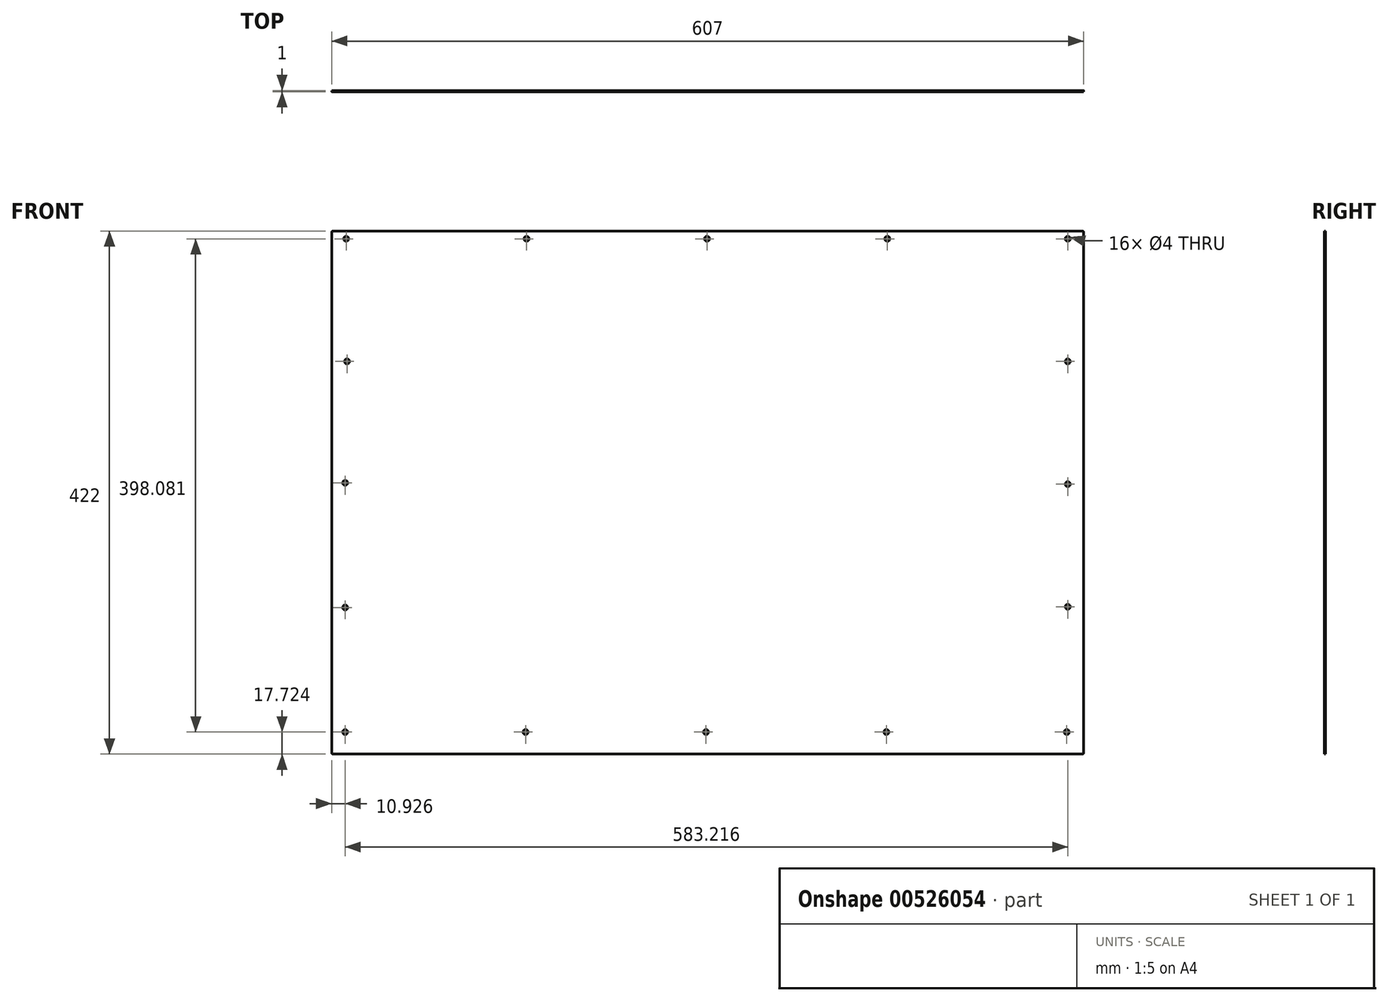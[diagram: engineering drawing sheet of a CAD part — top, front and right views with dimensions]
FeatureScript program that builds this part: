
annotation { "Feature Type Name" : "Feature", "Feature Type Description" : "" }
export const myFeature = defineFeature(function(context is Context, id is Id, definition is map)
    precondition{}
    {
        {
            var Q0;
            Q0=qCreatedBy(makeId("Front.planeOp"),FACE);
            var sketch = newSketch(context, id + "F0", { "sketchPlane" : qUnion([Q0])});
            skLineSegment(sketch, "E0.bottom", {"start": v(-558.83, 384.34) * mm, "end": v(46.17, 384.34) * mm});
            skLineSegment(sketch, "E0.top", {"start": v(-558.83, -37.66) * mm, "end": v(46.17, -37.66) * mm});
            skLineSegment(sketch, "E0.left", {"start": v(-559.83, 383.34) * mm, "end": v(-559.83, -36.66) * mm});
            skLineSegment(sketch, "E0.right", {"start": v(47.17, 383.34) * mm, "end": v(47.17, -36.66) * mm});
            skCircle(sketch, "E1", {"center": v(34.31, 378.15) * mm, "radius": 2 * mm});
            skCircle(sketch, "E2.0.1.0", {"center": v(34.31, 279.15) * mm, "radius": 2 * mm});
            skCircle(sketch, "E2.0.2.0", {"center": v(34.31, 180.15) * mm, "radius": 2 * mm});
            skCircle(sketch, "E2.0.3.0", {"center": v(34.31, 81.15) * mm, "radius": 2 * mm});
            skLineSegment(sketch, "E2.direction1", {"start": v(34.31, 378.15) * mm, "end": v(59.67, 378.15) * mm, "construction": true});
            skLineSegment(sketch, "E2.direction2", {"start": v(34.31, 378.15) * mm, "end": v(34.31, 279.15) * mm, "construction": true});
            skCircle(sketch, "E3.1.0.0", {"center": v(-111.29, 378.15) * mm, "radius": 2 * mm});
            skCircle(sketch, "E3.2.0.0", {"center": v(-256.89, 378.15) * mm, "radius": 2 * mm});
            skCircle(sketch, "E3.3.0.0", {"center": v(-402.49, 378.15) * mm, "radius": 2 * mm});
            skCircle(sketch, "E3.4.0.0", {"center": v(-548.09, 378.15) * mm, "radius": 2 * mm});
            skLineSegment(sketch, "E3.direction1", {"start": v(34.31, 378.15) * mm, "end": v(-111.29, 378.15) * mm, "construction": true});
            skCircle(sketch, "E4.0.1.0", {"center": v(-548.9, 181.22) * mm, "radius": 2 * mm});
            skCircle(sketch, "E4.0.2.0", {"center": v(-548.9, 80.64) * mm, "radius": 2 * mm});
            skCircle(sketch, "E4.0.3.0", {"center": v(-548.9, -19.94) * mm, "radius": 2 * mm});
            skCircle(sketch, "E5.1.0.0", {"center": v(-403.3, -19.94) * mm, "radius": 2 * mm});
            skCircle(sketch, "E5.2.0.0", {"center": v(-257.7, -19.94) * mm, "radius": 2 * mm});
            skCircle(sketch, "E5.3.0.0", {"center": v(-112.1, -19.94) * mm, "radius": 2 * mm});
            skCircle(sketch, "E5.4.0.0", {"center": v(33.5, -19.94) * mm, "radius": 2 * mm});
            skLineSegment(sketch, "E5.direction1", {"start": v(-548.9, -19.94) * mm, "end": v(-403.3, -19.94) * mm, "construction": true});
            skPoint(sketch, "E6.visualSharp", {"position": v(-559.83, 384.34) * mm});
            skArc(sketch, "E6.filletArc", {"start": v(-558.83, 384.34) * mm, "mid": v(-559.53, 384.05) * mm, "end": v(-559.83, 383.34) * mm});
            skPoint(sketch, "E7.visualSharp", {"position": v(-559.83, -37.66) * mm});
            skArc(sketch, "E7.filletArc", {"start": v(-559.83, -36.66) * mm, "mid": v(-559.53, -37.36) * mm, "end": v(-558.83, -37.66) * mm});
            skPoint(sketch, "E8.visualSharp", {"position": v(47.17, 384.34) * mm});
            skArc(sketch, "E8.filletArc", {"start": v(47.17, 383.34) * mm, "mid": v(46.88, 384.05) * mm, "end": v(46.17, 384.34) * mm});
            skPoint(sketch, "E9.visualSharp", {"position": v(47.17, -37.66) * mm});
            skArc(sketch, "E9.filletArc", {"start": v(46.17, -37.66) * mm, "mid": v(46.88, -37.36) * mm, "end": v(47.17, -36.66) * mm});
            skCircle(sketch, "E10.0.1.0", {"center": v(-547.4, 279.15) * mm, "radius": 2 * mm});
            skLineSegment(sketch, "E11", {"start": v(34.31, 279.15) * mm, "end": v(-683.7, 279.15) * mm, "construction": true});
            skSolve(sketch);
        }
        {
            var Q0;
            Q0=makeQuery(id+"F0.imprint","IMPRINT",FACE,{"disambiguationData":[TD([[makeQuery(id+"F0.imprint","IMPRINT",EDGE,{"derivedFrom":sQuery(id+"F0.wireOp",EDGE,"E0.bottom")}),-1.0]])]});
            extrude(context, id + "F1", {"entities" : qUnion([Q0]), "depth" : 1 * mm, "offsetDistance" : 25 * mm});
        }
    });
